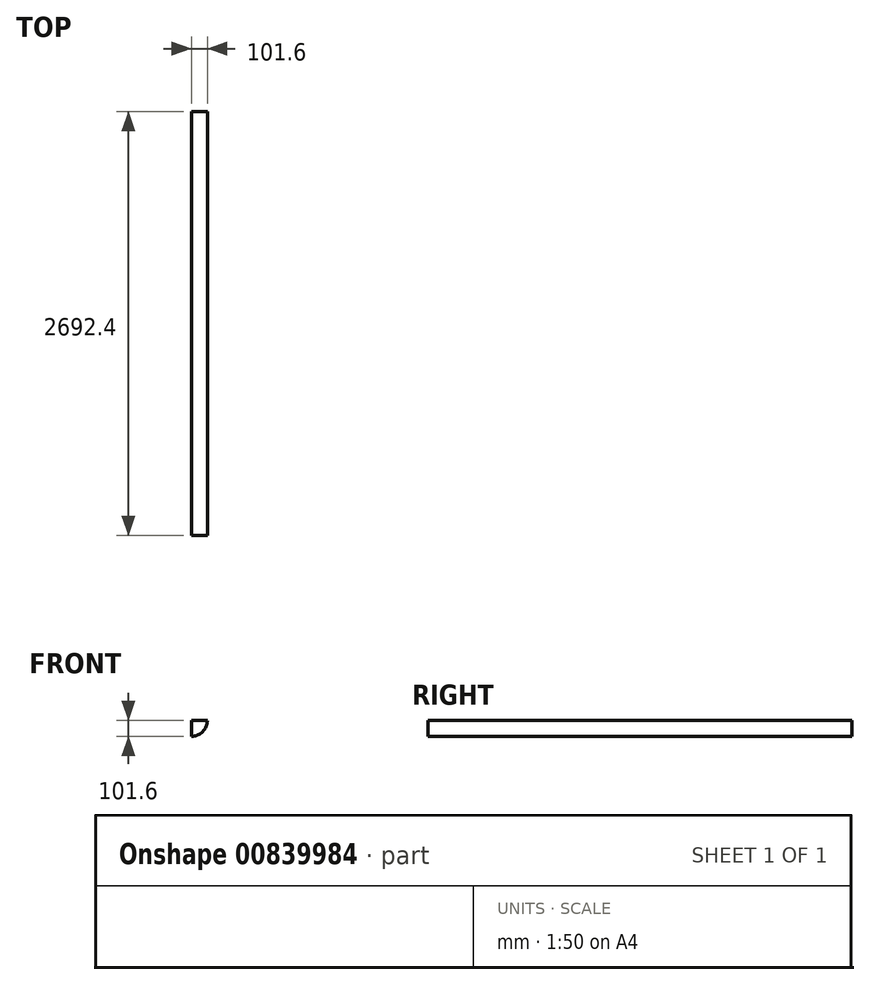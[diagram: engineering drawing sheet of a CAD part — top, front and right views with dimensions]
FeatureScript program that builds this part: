
annotation { "Feature Type Name" : "Feature", "Feature Type Description" : "" }
export const myFeature = defineFeature(function(context is Context, id is Id, definition is map)
    precondition{}
    {
        {
            var Q0;
            Q0=qCreatedBy(makeId("Front.planeOp"),FACE);
            var sketch = newSketch(context, id + "F0", { "sketchPlane" : qUnion([Q0])});
            skArc(sketch, "E0", {"start": v(0, -101.6) * mm, "mid": v(71.84, -71.84) * mm, "end": v(101.6, 0) * mm});
            skLineSegment(sketch, "E1", {"start": v(0, 0) * mm, "end": v(101.6, 0) * mm});
            skLineSegment(sketch, "E2", {"start": v(0, 0) * mm, "end": v(0, -101.6) * mm});
            skSolve(sketch);
        }
        {
            var Q0;
            Q0 = qSketchRegion(id + "F0", true);
            extrude(context, id + "F1", {"entities" : qUnion([Q0]), "depth" : 2692.4 * mm, "offsetDistance" : 25.4 * mm});
        }
    });
